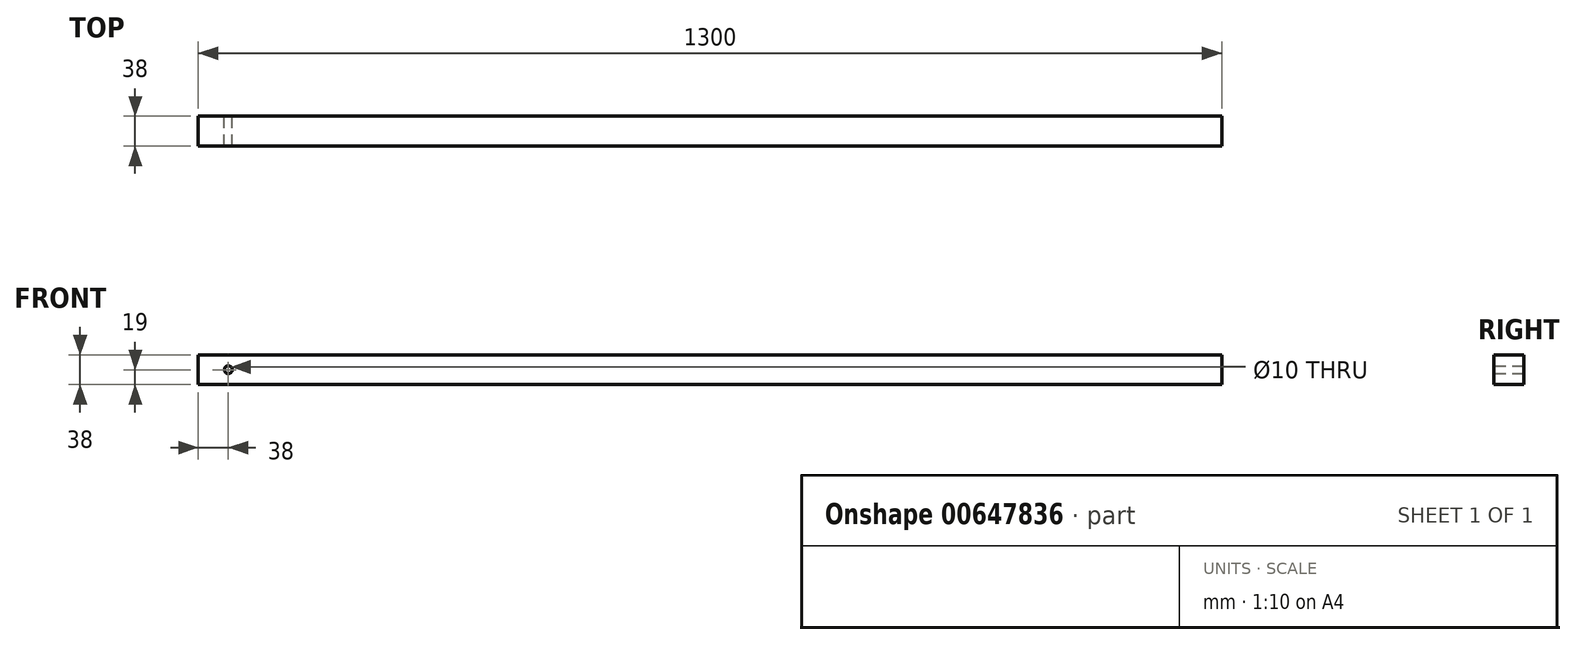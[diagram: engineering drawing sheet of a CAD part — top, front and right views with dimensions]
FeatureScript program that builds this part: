
annotation { "Feature Type Name" : "Feature", "Feature Type Description" : "" }
export const myFeature = defineFeature(function(context is Context, id is Id, definition is map)
    precondition{}
    {
        {
            var Q0;
            Q0=qCreatedBy(makeId("Front.planeOp"),FACE);
            var sketch = newSketch(context, id + "F0", { "sketchPlane" : qUnion([Q0])});
            skLineSegment(sketch, "E0.bottom", {"start": v(-650, 19) * mm, "end": v(650, 19) * mm});
            skLineSegment(sketch, "E0.top", {"start": v(-650, -19) * mm, "end": v(650, -19) * mm});
            skLineSegment(sketch, "E0.left", {"start": v(-650, 19) * mm, "end": v(-650, -19) * mm});
            skLineSegment(sketch, "E0.right", {"start": v(650, 19) * mm, "end": v(650, -19) * mm});
            skPoint(sketch, "E0.middle", {"position": v(0, 0) * mm});
            skPoint(sketch, "E1", {"position": v(-612, 0) * mm});
            skSolve(sketch);
        }
        {
            var Q0;
            Q0 = qSketchRegion(id + "F0", true);
            extrude(context, id + "F1", {"entities" : qUnion([Q0]), "depth" : 38 * mm, "offsetDistance" : 25 * mm});
        }
        {
            var Q0;
            Q0=sQuery(id+"F0.wireOp",VERTEX,"E1");
            var Q1;
            Q1=makeQuery(id+"F1.opExtrude","SWEPT_BODY",BODY,{"disambiguationData":[OSD([sQuery(id+"F0.wireOp",EDGE,"E0.bottom"),sQuery(id+"F0.wireOp",EDGE,"E0.top"),sQuery(id+"F0.wireOp",EDGE,"E0.left"),sQuery(id+"F0.wireOp",EDGE,"E0.right")])]});
            hole(context, id + "F2", {"style" : HoleStyle.SIMPLE, "endStyle" : HoleEndStyle.THROUGH, "oppositeDirection" : true, "holeDiameter" : 10 * mm, "majorDiameter" : 5 * mm, "isTappedThrough" : true, "tappedDepth" : 12 * mm, "tapClearance" : 3, "locations" : qUnion([Q0]), "scope" : qUnion([Q1])});
        }
    });
